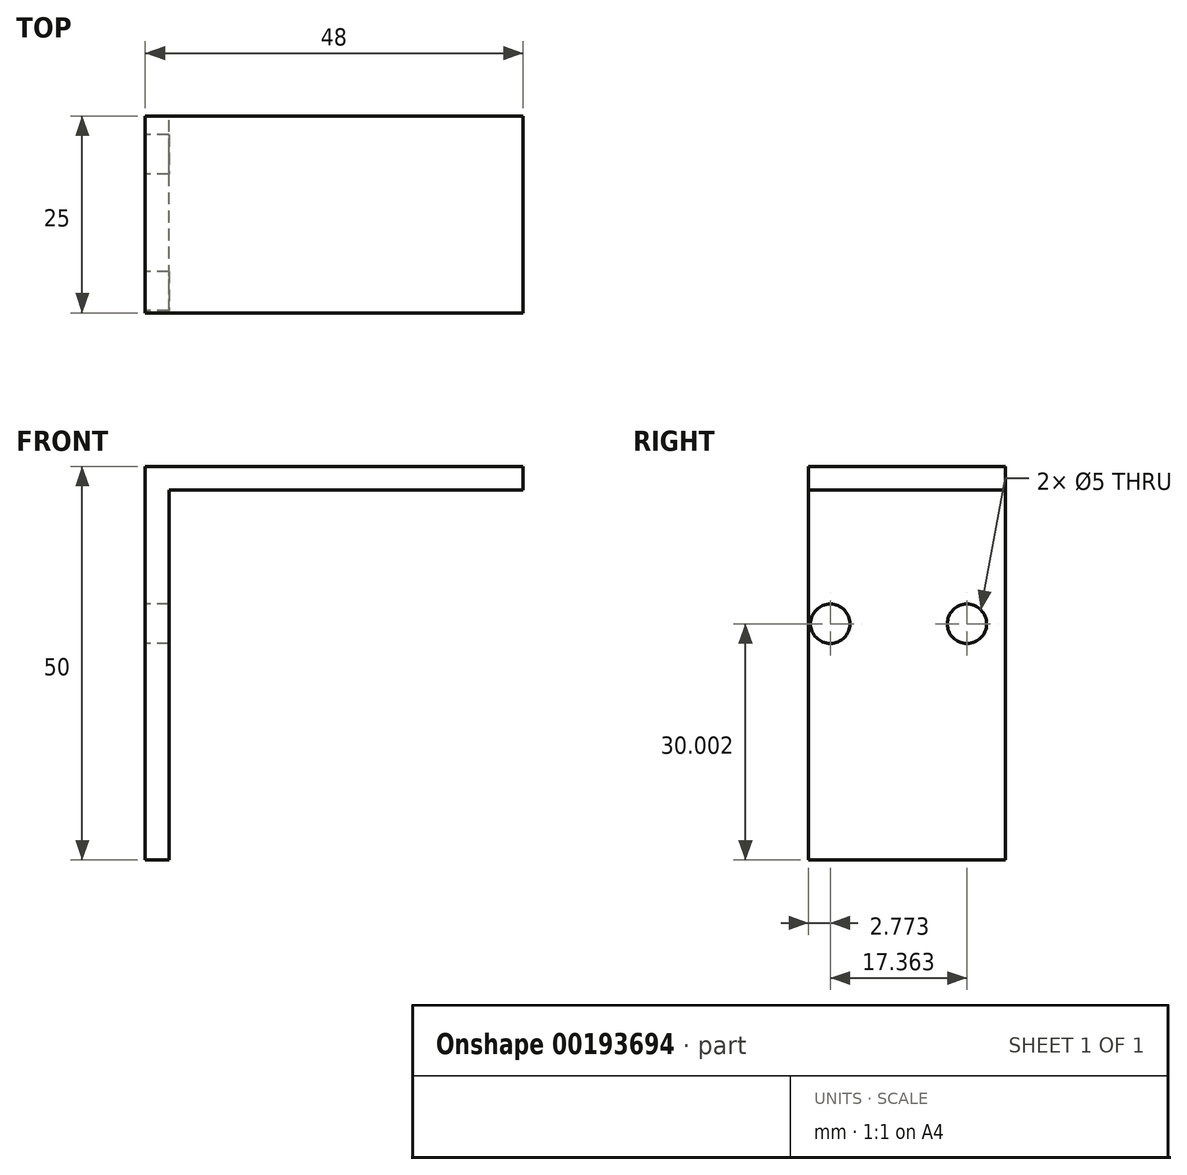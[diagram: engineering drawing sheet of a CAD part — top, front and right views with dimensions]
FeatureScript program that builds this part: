
annotation { "Feature Type Name" : "Feature", "Feature Type Description" : "" }
export const myFeature = defineFeature(function(context is Context, id is Id, definition is map)
    precondition{}
    {
        {
            var Q0;
            Q0=qCreatedBy(makeId("Front.planeOp"),FACE);
            var sketch = newSketch(context, id + "F0", { "sketchPlane" : qUnion([Q0])});
            skLineSegment(sketch, "E0", {"start": v(-32.96, 20.08) * mm, "end": v(-32.96, -29.92) * mm});
            skLineSegment(sketch, "E1", {"start": v(-32.96, -29.92) * mm, "end": v(-29.96, -29.92) * mm});
            skLineSegment(sketch, "E2", {"start": v(-29.96, -29.92) * mm, "end": v(-29.96, 17.08) * mm});
            skLineSegment(sketch, "E3", {"start": v(-29.96, 17.08) * mm, "end": v(15.04, 17.08) * mm});
            skLineSegment(sketch, "E4", {"start": v(15.04, 17.08) * mm, "end": v(15.04, 20.08) * mm});
            skLineSegment(sketch, "E5", {"start": v(15.04, 20.08) * mm, "end": v(-32.96, 20.08) * mm});
            skSolve(sketch);
        }
        {
            var Q0;
            Q0 = qSketchRegion(id + "F0", true);
            extrude(context, id + "F1", {"entities" : qUnion([Q0]), "depth" : 25 * mm});
        }
        {
            var Q0;
            Q0=makeQuery(id+"F1.opExtrude","SWEPT_FACE",FACE,{"disambiguationData":[OSD([sQuery(id+"F0.wireOp",EDGE,"E0")])]});
            var sketch = newSketch(context, id + "F2", { "sketchPlane" : qUnion([Q0])});
            skCircle(sketch, "E6", {"center": v(22.23, 0.08) * mm, "radius": 2.5 * mm});
            skCircle(sketch, "E7", {"center": v(4.86, 0.08) * mm, "radius": 2.5 * mm});
            skSolve(sketch);
        }
        {
            var Q0;
            Q0=makeQuery(id+"F2.imprint","IMPRINT",FACE,{"disambiguationData":[TD([[makeQuery(id+"F2.imprint","IMPRINT",EDGE,{"derivedFrom":sQuery(id+"F2.wireOp",EDGE,"E6")}),1.0]])]});
            var Q1;
            Q1=makeQuery(id+"F2.imprint","IMPRINT",FACE,{"disambiguationData":[TD([[makeQuery(id+"F2.imprint","IMPRINT",EDGE,{"derivedFrom":sQuery(id+"F2.wireOp",EDGE,"E7")}),1.0]])]});
            extrude(context, id + "F3", {"entities" : qUnion([Q0, Q1]), "operationType" : NewBodyOperationType.REMOVE, "oppositeDirection" : true, "depth" : 25 * mm});
        }
    });
